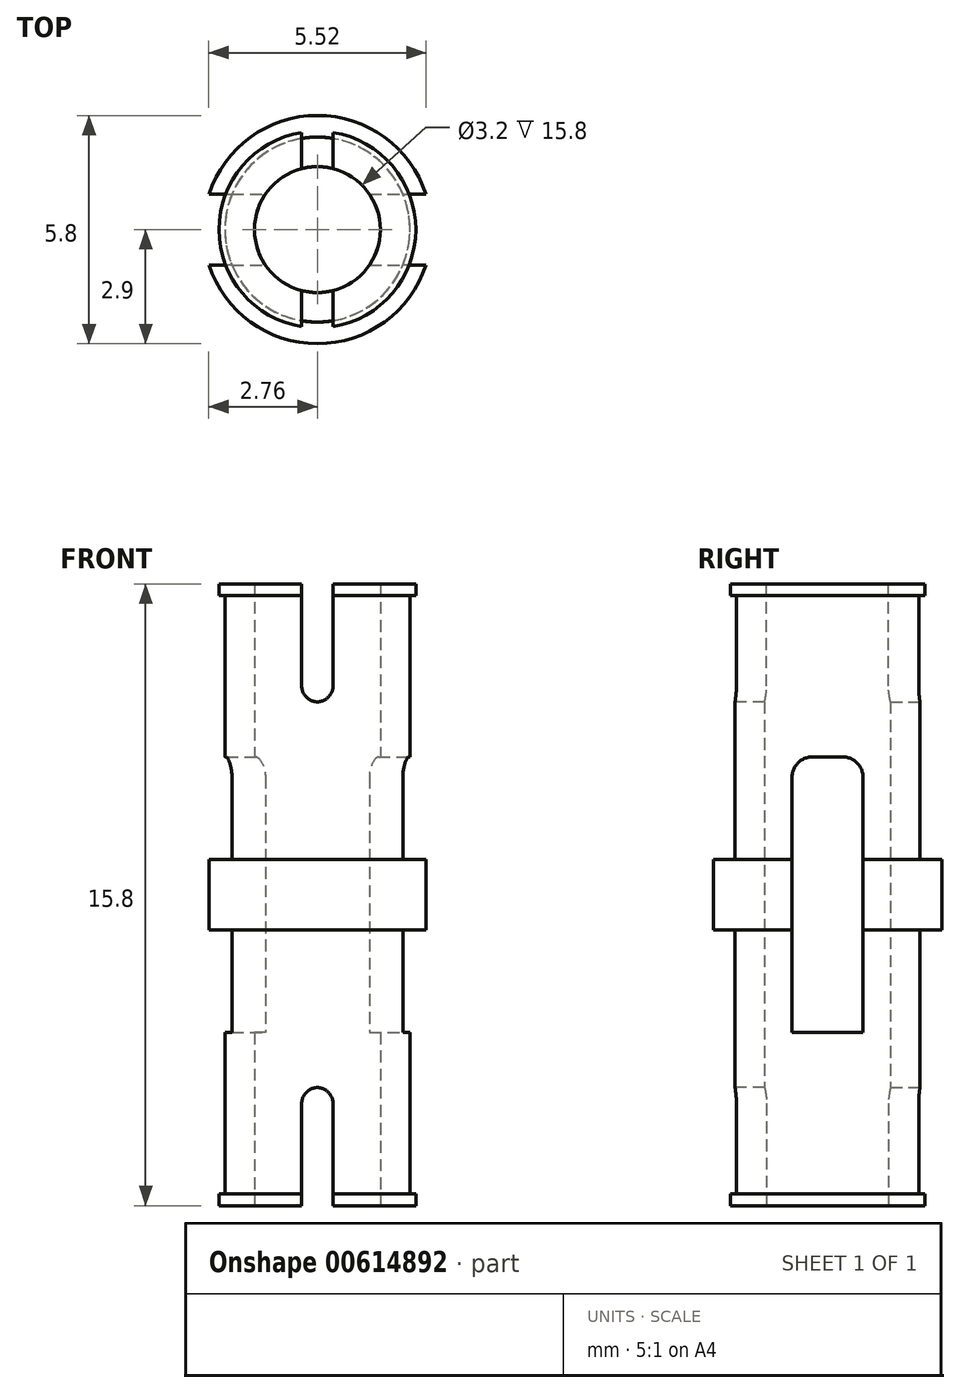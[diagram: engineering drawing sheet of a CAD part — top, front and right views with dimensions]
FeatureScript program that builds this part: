
annotation { "Feature Type Name" : "Feature", "Feature Type Description" : "" }
export const myFeature = defineFeature(function(context is Context, id is Id, definition is map)
    precondition{}
    {
        {
            var Q0;
            Q0=qCreatedBy(makeId("Top.planeOp"),FACE);
            var sketch = newSketch(context, id + "F0", { "sketchPlane" : qUnion([Q0])});
            skCircle(sketch, "E0", {"center": v(0, 0) * mm, "radius": 2.35 * mm});
            skCircle(sketch, "E1", {"center": v(0, 0) * mm, "radius": 2.9 * mm});
            skCircle(sketch, "E2", {"center": v(0, 0) * mm, "radius": 1.6 * mm});
            skSolve(sketch);
        }
        {
            var Q0;
            Q0=makeQuery(id+"F0.imprint","IMPRINT",FACE,{"disambiguationData":[TD([[makeQuery(id+"F0.imprint","IMPRINT",EDGE,{"derivedFrom":sQuery(id+"F0.wireOp",EDGE,"E0")}),1.0]])]});
            extrude(context, id + "F1", {"entities" : qUnion([Q0]), "endBound" : BoundingType.SYMMETRIC, "depth" : 15.8 * mm, "offsetDistance" : 25 * mm});
        }
        {
            var Q0;
            Q0=makeQuery(id+"F1.opExtrude","CAP_FACE",FACE,{"disambiguationData":[OSD([sQuery(id+"F0.wireOp",EDGE,"E0"),sQuery(id+"F0.wireOp",EDGE,"r6Cq1YDG-hLj7-gypi-DKDx-Uv785pJpsHHv")])],"isStart":false});
            var sketch = newSketch(context, id + "F2", { "sketchPlane" : qUnion([Q0])});
            skLineSegment(sketch, "E3", {"start": v(0, 0) * mm, "end": v(0, 1.6) * mm});
            skLineSegment(sketch, "E4", {"start": v(0, 0) * mm, "end": v(0, -1.6) * mm});
            skLineSegment(sketch, "E5", {"start": v(-0.4, -1.6) * mm, "end": v(-0.4, -2.32) * mm});
            skLineSegment(sketch, "E6", {"start": v(0.4, -1.6) * mm, "end": v(0.4, -2.32) * mm});
            skLineSegment(sketch, "E7", {"start": v(0.4, -1.6) * mm, "end": v(0.4, -1.55) * mm});
            skLineSegment(sketch, "E8", {"start": v(-0.4, -1.6) * mm, "end": v(-0.4, -1.55) * mm});
            skLineSegment(sketch, "E9", {"start": v(-3.52, 0) * mm, "end": v(4.39, 0) * mm, "construction": true});
            skLineSegment(sketch, "E10.MirrorCS", {"start": v(-0.4, 1.6) * mm, "end": v(-0.4, 2.32) * mm});
            skLineSegment(sketch, "E11.MirrorCS", {"start": v(0.4, 1.6) * mm, "end": v(0.4, 2.32) * mm});
            skLineSegment(sketch, "E12.MirrorCS", {"start": v(0.4, 1.6) * mm, "end": v(0.4, 1.55) * mm});
            skLineSegment(sketch, "E13.MirrorCS", {"start": v(-0.4, 1.6) * mm, "end": v(-0.4, 1.55) * mm});
            skSolve(sketch);
        }
        {
            var Q0;
            {var subQ3=sQuery(id+"F2.wireOp",EDGE,"E10.MirrorCS");Q0=makeQuery(id+"F2.imprint","IMPRINT",FACE,{"disambiguationData":[TD([[makeQuery(id+"F2.imprint","IMPRINT",EDGE,{"derivedFrom":subQ3}),-1.0]])]});}
            var Q1;
            {var subQ5=sQuery(id+"F2.wireOp",EDGE,"E5");Q1=makeQuery(id+"F2.imprint","IMPRINT",FACE,{"disambiguationData":[TD([[makeQuery(id+"F2.imprint","IMPRINT",EDGE,{"derivedFrom":subQ5}),1.0]])]});}
            extrude(context, id + "F3", {"entities" : qUnion([Q0, Q1]), "operationType" : NewBodyOperationType.REMOVE, "oppositeDirection" : true, "depth" : 3 * mm, "offsetDistance" : 25 * mm});
        }
        {
            var Q0;
            Q0=makeQuery(id+"F0.imprint","IMPRINT",FACE,{"disambiguationData":[TD([[makeQuery(id+"F0.imprint","IMPRINT",EDGE,{"derivedFrom":sQuery(id+"F0.wireOp",EDGE,"E0")}),-1.0]])]});
            extrude(context, id + "F4", {"entities" : qUnion([Q0]), "operationType" : NewBodyOperationType.ADD, "endBound" : BoundingType.SYMMETRIC, "depth" : 1.8 * mm, "offsetDistance" : 25 * mm});
        }
        {
            var Q0;
            Q0=qCreatedBy(makeId("Right.planeOp"),FACE);
            var sketch = newSketch(context, id + "F5", { "sketchPlane" : qUnion([Q0])});
            skLineSegment(sketch, "E14", {"start": v(0.9, 3.5) * mm, "end": v(0.9, -3.5) * mm});
            skLineSegment(sketch, "E15", {"start": v(-0.9, -3.5) * mm, "end": v(-0.9, 3.5) * mm});
            skLineSegment(sketch, "E16", {"start": v(-0.9, 3.5) * mm, "end": v(0.9, 3.5) * mm});
            skLineSegment(sketch, "E17", {"start": v(-0.9, -3.5) * mm, "end": v(0.9, -3.5) * mm});
            skLineSegment(sketch, "E18", {"start": v(0.9, -3.5) * mm, "end": v(-0.9, -3.5) * mm});
            skSolve(sketch);
        }
        {
            var Q0;
            Q0 = qSketchRegion(id + "F5", true);
            extrude(context, id + "F6", {"entities" : qUnion([Q0]), "operationType" : NewBodyOperationType.REMOVE, "endBound" : BoundingType.SYMMETRIC, "oppositeDirection" : true, "depth" : 25 * mm, "offsetDistance" : 25 * mm});
        }
        {
            var Q0;
            Q0=makeQuery(id+"F6.boolean.opBoolean","COPY",EDGE,{"disambiguationData":[OD(1.0)],"derivedFrom":makeQuery(id+"F6.opExtrude","SWEPT_EDGE",EDGE,{"disambiguationData":[OSD([sQuery(id+"F5.wireOp",EDGE,"E15"),sQuery(id+"F5.wireOp",EDGE,"E16")])]})});
            var Q1;
            Q1=makeQuery(id+"F6.boolean.opBoolean","COPY",EDGE,{"disambiguationData":[OD(1.0)],"derivedFrom":makeQuery(id+"F6.opExtrude","SWEPT_EDGE",EDGE,{"disambiguationData":[OSD([sQuery(id+"F5.wireOp",EDGE,"E14"),sQuery(id+"F5.wireOp",EDGE,"E16")])]})});
            var Q2;
            Q2=makeQuery(id+"F6.boolean.opBoolean","COPY",EDGE,{"disambiguationData":[OD(1.0)],"derivedFrom":makeQuery(id+"F6.opExtrude","SWEPT_EDGE",EDGE,{"disambiguationData":[OSD([sQuery(id+"F5.wireOp",EDGE,"E15"),sQuery(id+"F5.wireOp",EDGE,"E18")])]})});
            var Q3;
            Q3=makeQuery(id+"F6.boolean.opBoolean","COPY",EDGE,{"disambiguationData":[OD(1.0)],"derivedFrom":makeQuery(id+"F6.opExtrude","SWEPT_EDGE",EDGE,{"disambiguationData":[OSD([sQuery(id+"F5.wireOp",EDGE,"E14"),sQuery(id+"F5.wireOp",EDGE,"E18")])]})});
            var Q4;
            Q4=makeQuery(id+"F6.boolean.opBoolean","COPY",EDGE,{"disambiguationData":[OD(0.0)],"derivedFrom":makeQuery(id+"F6.opExtrude","SWEPT_EDGE",EDGE,{"disambiguationData":[OSD([sQuery(id+"F5.wireOp",EDGE,"E14"),sQuery(id+"F5.wireOp",EDGE,"E18")])]})});
            var Q5;
            Q5=makeQuery(id+"F6.boolean.opBoolean","COPY",EDGE,{"disambiguationData":[OD(0.0)],"derivedFrom":makeQuery(id+"F6.opExtrude","SWEPT_EDGE",EDGE,{"disambiguationData":[OSD([sQuery(id+"F5.wireOp",EDGE,"E15"),sQuery(id+"F5.wireOp",EDGE,"E18")])]})});
            var Q6;
            Q6=makeQuery(id+"F6.boolean.opBoolean","COPY",EDGE,{"disambiguationData":[OD(0.0)],"derivedFrom":makeQuery(id+"F6.opExtrude","SWEPT_EDGE",EDGE,{"disambiguationData":[OSD([sQuery(id+"F5.wireOp",EDGE,"E15"),sQuery(id+"F5.wireOp",EDGE,"E16")])]})});
            var Q7;
            Q7=makeQuery(id+"F6.boolean.opBoolean","COPY",EDGE,{"disambiguationData":[OD(0.0)],"derivedFrom":makeQuery(id+"F6.opExtrude","SWEPT_EDGE",EDGE,{"disambiguationData":[OSD([sQuery(id+"F5.wireOp",EDGE,"E14"),sQuery(id+"F5.wireOp",EDGE,"E16")])]})});
            fillet(context, id + "F7", {"entities" : qUnion([Q0, Q1, Q2, Q3, Q4, Q5, Q6, Q7]), "radius" : 0.5 * mm, "tangentPropagation" : true, "allowEdgeOverflow" : false});
        }
        {
            var Q0;
            Q0=makeQuery(id+"F1.opExtrude","CAP_FACE",FACE,{"disambiguationData":[OSD([sQuery(id+"F0.wireOp",EDGE,"E0"),sQuery(id+"F0.wireOp",EDGE,"E2")])],"isStart":true});
            var sketch = newSketch(context, id + "F8", { "sketchPlane" : qUnion([Q0])});
            skLineSegment(sketch, "E19", {"start": v(0, 0) * mm, "end": v(0, 1.6) * mm, "construction": true});
            skLineSegment(sketch, "E20", {"start": v(0.4, 1.6) * mm, "end": v(0.4, 2.32) * mm});
            skLineSegment(sketch, "E21", {"start": v(-0.4, 1.6) * mm, "end": v(-0.4, 2.32) * mm});
            skLineSegment(sketch, "E22", {"start": v(-0.4, 1.6) * mm, "end": v(-0.4, 1.55) * mm});
            skLineSegment(sketch, "E23", {"start": v(0.4, 1.6) * mm, "end": v(0.4, 1.55) * mm});
            skLineSegment(sketch, "E24", {"start": v(-3.6, 0) * mm, "end": v(3.75, 0) * mm, "construction": true});
            skLineSegment(sketch, "E25.MirrorCS", {"start": v(-0.4, -1.6) * mm, "end": v(-0.4, -2.32) * mm});
            skLineSegment(sketch, "E26.MirrorCS", {"start": v(0.4, -1.6) * mm, "end": v(0.4, -2.32) * mm});
            skLineSegment(sketch, "E27.MirrorCS", {"start": v(-0.4, -1.6) * mm, "end": v(-0.4, -1.55) * mm});
            skLineSegment(sketch, "E28.MirrorCS", {"start": v(0.4, -1.6) * mm, "end": v(0.4, -1.55) * mm});
            skSolve(sketch);
        }
        {
            var Q0;
            {var subQ4=sQuery(id+"F8.wireOp",EDGE,"E20");Q0=makeQuery(id+"F8.imprint","IMPRINT",FACE,{"disambiguationData":[TD([[makeQuery(id+"F8.imprint","IMPRINT",EDGE,{"derivedFrom":subQ4}),1.0]])]});}
            var Q1;
            {var subQ3=sQuery(id+"F8.wireOp",EDGE,"E25.MirrorCS");Q1=makeQuery(id+"F8.imprint","IMPRINT",FACE,{"disambiguationData":[TD([[makeQuery(id+"F8.imprint","IMPRINT",EDGE,{"derivedFrom":subQ3}),1.0]])]});}
            extrude(context, id + "F9", {"entities" : qUnion([Q0, Q1]), "operationType" : NewBodyOperationType.REMOVE, "oppositeDirection" : true, "depth" : 3 * mm, "offsetDistance" : 25 * mm});
        }
        {
            var Q0;
            Q0=makeQuery(id+"F9.boolean.opBoolean","COPY",EDGE,{"derivedFrom":makeQuery(id+"F9.opExtrude","CAP_EDGE",EDGE,{"disambiguationData":[OSD([sQuery(id+"F8.wireOp",EDGE,"E20"),sQuery(id+"F8.wireOp",EDGE,"E23")])],"isStart":false})});
            var Q1;
            Q1=makeQuery(id+"F9.boolean.opBoolean","COPY",EDGE,{"derivedFrom":makeQuery(id+"F9.opExtrude","CAP_EDGE",EDGE,{"disambiguationData":[OSD([sQuery(id+"F8.wireOp",EDGE,"E21"),sQuery(id+"F8.wireOp",EDGE,"E22")])],"isStart":false})});
            var Q2;
            Q2=makeQuery(id+"F9.boolean.opBoolean","COPY",EDGE,{"derivedFrom":makeQuery(id+"F9.opExtrude","CAP_EDGE",EDGE,{"disambiguationData":[OSD([sQuery(id+"F8.wireOp",EDGE,"E25.MirrorCS"),sQuery(id+"F8.wireOp",EDGE,"E27.MirrorCS")])],"isStart":false})});
            var Q3;
            Q3=makeQuery(id+"F9.boolean.opBoolean","COPY",EDGE,{"derivedFrom":makeQuery(id+"F9.opExtrude","CAP_EDGE",EDGE,{"disambiguationData":[OSD([sQuery(id+"F8.wireOp",EDGE,"E26.MirrorCS"),sQuery(id+"F8.wireOp",EDGE,"E28.MirrorCS")])],"isStart":false})});
            var Q4;
            Q4=makeQuery(id+"F3.boolean.opBoolean","COPY",EDGE,{"derivedFrom":makeQuery(id+"F3.opExtrude","CAP_EDGE",EDGE,{"disambiguationData":[OSD([sQuery(id+"F2.wireOp",EDGE,"E11.MirrorCS"),sQuery(id+"F2.wireOp",EDGE,"E12.MirrorCS")])],"isStart":false})});
            var Q5;
            Q5=makeQuery(id+"F3.boolean.opBoolean","COPY",EDGE,{"derivedFrom":makeQuery(id+"F3.opExtrude","CAP_EDGE",EDGE,{"disambiguationData":[OSD([sQuery(id+"F2.wireOp",EDGE,"E10.MirrorCS"),sQuery(id+"F2.wireOp",EDGE,"E13.MirrorCS")])],"isStart":false})});
            var Q6;
            Q6=makeQuery(id+"F3.boolean.opBoolean","COPY",EDGE,{"derivedFrom":makeQuery(id+"F3.opExtrude","CAP_EDGE",EDGE,{"disambiguationData":[OSD([sQuery(id+"F2.wireOp",EDGE,"E5"),sQuery(id+"F2.wireOp",EDGE,"E8")])],"isStart":false})});
            var Q7;
            Q7=makeQuery(id+"F3.boolean.opBoolean","COPY",EDGE,{"derivedFrom":makeQuery(id+"F3.opExtrude","CAP_EDGE",EDGE,{"disambiguationData":[OSD([sQuery(id+"F2.wireOp",EDGE,"E6"),sQuery(id+"F2.wireOp",EDGE,"E7")])],"isStart":false})});
            fillet(context, id + "F10", {"entities" : qUnion([Q0, Q1, Q2, Q3, Q4, Q5, Q6, Q7]), "radius" : 0.4 * mm, "tangentPropagation" : true, "allowEdgeOverflow" : false});
        }
        {
            var Q0;
            {var subQ0=sQuery(id+"F0.wireOp",EDGE,"E0");var subQ1=sQuery(id+"F0.wireOp",EDGE,"E2");Q0=makeQuery(id+"F9.boolean.opBoolean","SPLIT",FACE,{"disambiguationData":[TD([makeQuery(id+"F9.opExtrude","SWEPT_FACE",FACE,{"disambiguationData":[OSD([sQuery(id+"F8.wireOp",EDGE,"E21"),sQuery(id+"F8.wireOp",EDGE,"E22")])]})])],"derivedFrom":makeQuery(id+"F1.opExtrude","CAP_FACE",FACE,{"disambiguationData":[OSD([subQ0,subQ1])],"isStart":true})});}
            var sketch = newSketch(context, id + "F11", { "sketchPlane" : qUnion([Q0])});
            skCircle(sketch, "E29", {"center": v(0, 0) * mm, "radius": 2.5 * mm});
            skCircle(sketch, "E30", {"center": v(0, 0) * mm, "radius": 2.35 * mm});
            skLineSegment(sketch, "E31", {"start": v(-0.4, 2.32) * mm, "end": v(-0.4, 2.47) * mm});
            skLineSegment(sketch, "E32.MirrorCS", {"start": v(0.4, 2.32) * mm, "end": v(0.4, 2.47) * mm});
            skLineSegment(sketch, "E33.MirrorCS", {"start": v(-0.4, -2.32) * mm, "end": v(-0.4, -2.47) * mm});
            skLineSegment(sketch, "E34.MirrorCS", {"start": v(0.4, -2.32) * mm, "end": v(0.4, -2.47) * mm});
            skSolve(sketch);
        }
        {
            var Q0;
            {var subQ0=sQuery(id+"F11.wireOp",EDGE,"E31");Q0=makeQuery(id+"F11.imprint","IMPRINT",FACE,{"disambiguationData":[TD([[makeQuery(id+"F11.imprint","IMPRINT",EDGE,{"derivedFrom":subQ0}),1.0]])]});}
            var Q1;
            {var subQ0=sQuery(id+"F11.wireOp",EDGE,"E32.MirrorCS");Q1=makeQuery(id+"F11.imprint","IMPRINT",FACE,{"disambiguationData":[TD([[makeQuery(id+"F11.imprint","IMPRINT",EDGE,{"derivedFrom":subQ0}),-1.0]])]});}
            extrude(context, id + "F12", {"entities" : qUnion([Q0, Q1]), "operationType" : NewBodyOperationType.ADD, "oppositeDirection" : true, "depth" : 0.3 * mm, "offsetDistance" : 25 * mm});
        }
        {
            var Q0;
            {var subQ0=sQuery(id+"F0.wireOp",EDGE,"E0");var subQ1=sQuery(id+"F0.wireOp",EDGE,"E2");Q0=makeQuery(id+"F3.boolean.opBoolean","SPLIT",FACE,{"disambiguationData":[TD([makeQuery(id+"F3.opExtrude","SWEPT_FACE",FACE,{"disambiguationData":[OSD([sQuery(id+"F2.wireOp",EDGE,"E5"),sQuery(id+"F2.wireOp",EDGE,"E8")])]})])],"derivedFrom":makeQuery(id+"F1.opExtrude","CAP_FACE",FACE,{"disambiguationData":[OSD([subQ0,subQ1])],"isStart":false})});}
            var sketch = newSketch(context, id + "F13", { "sketchPlane" : qUnion([Q0])});
            skCircle(sketch, "E35", {"center": v(0, 0) * mm, "radius": 2.5 * mm});
            skLineSegment(sketch, "E36", {"start": v(-0.4, -2.32) * mm, "end": v(-0.4, -2.47) * mm});
            skLineSegment(sketch, "E37", {"start": v(-0.4, 2.32) * mm, "end": v(-0.4, 2.47) * mm});
            skSolve(sketch);
        }
        {
            var Q0;
            {var subQ0=sQuery(id+"F13.wireOp",EDGE,"E36");Q0=makeQuery(id+"F13.imprint","IMPRINT",FACE,{"disambiguationData":[TD([[makeQuery(id+"F13.imprint","IMPRINT",EDGE,{"derivedFrom":subQ0}),-1.0]])]});}
            extrude(context, id + "F14", {"entities" : qUnion([Q0]), "operationType" : NewBodyOperationType.ADD, "oppositeDirection" : true, "depth" : 0.3 * mm, "offsetDistance" : 25 * mm});
        }
        {
            var Q0;
            {var subQ0=sQuery(id+"F0.wireOp",EDGE,"E0");var subQ1=sQuery(id+"F0.wireOp",EDGE,"E2");Q0=makeQuery(id+"F3.boolean.opBoolean","SPLIT",FACE,{"disambiguationData":[TD([makeQuery(id+"F3.opExtrude","SWEPT_FACE",FACE,{"disambiguationData":[OSD([sQuery(id+"F2.wireOp",EDGE,"E6"),sQuery(id+"F2.wireOp",EDGE,"E7")])]})])],"derivedFrom":makeQuery(id+"F1.opExtrude","CAP_FACE",FACE,{"disambiguationData":[OSD([subQ0,subQ1])],"isStart":false})});}
            var sketch = newSketch(context, id + "F15", { "sketchPlane" : qUnion([Q0])});
            skCircle(sketch, "E38", {"center": v(0, 0) * mm, "radius": 2.5 * mm});
            skLineSegment(sketch, "E39", {"start": v(0.4, -2.32) * mm, "end": v(0.4, -2.47) * mm});
            skLineSegment(sketch, "E40", {"start": v(0.4, 2.32) * mm, "end": v(0.4, 2.47) * mm});
            skSolve(sketch);
        }
        {
            var Q0;
            {var subQ0=sQuery(id+"F15.wireOp",EDGE,"E39");Q0=makeQuery(id+"F15.imprint","IMPRINT",FACE,{"disambiguationData":[TD([[makeQuery(id+"F15.imprint","IMPRINT",EDGE,{"derivedFrom":subQ0}),1.0]])]});}
            extrude(context, id + "F16", {"entities" : qUnion([Q0]), "operationType" : NewBodyOperationType.ADD, "oppositeDirection" : true, "depth" : 0.3 * mm, "offsetDistance" : 25 * mm});
        }
    });
